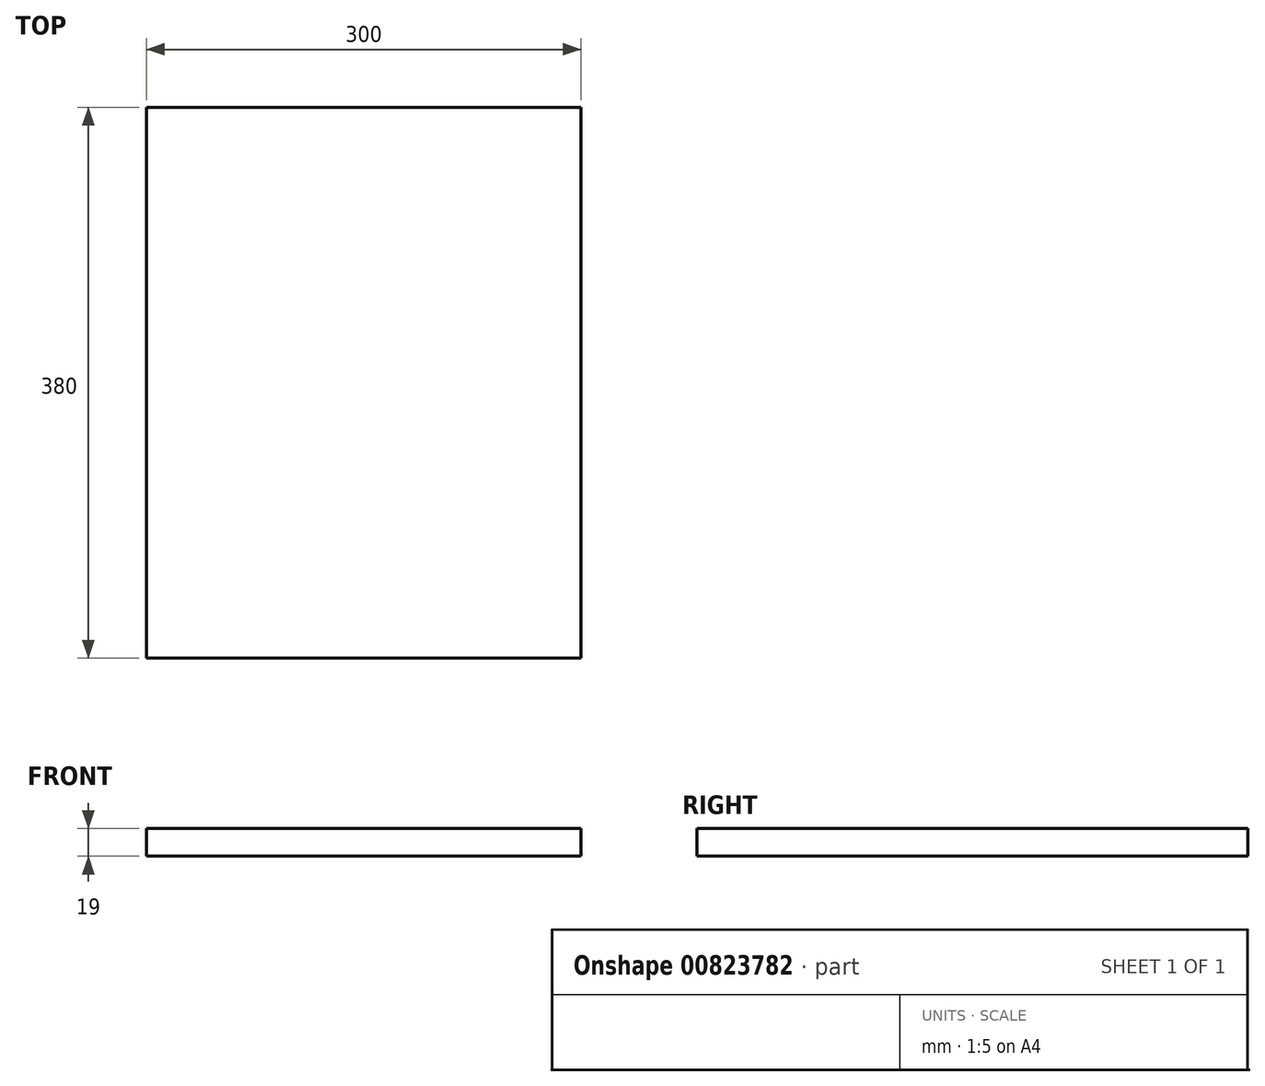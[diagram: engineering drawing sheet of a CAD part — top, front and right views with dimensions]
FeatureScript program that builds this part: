
annotation { "Feature Type Name" : "Feature", "Feature Type Description" : "" }
export const myFeature = defineFeature(function(context is Context, id is Id, definition is map)
    precondition{}
    {
        {
            var Q0;
            Q0=qCreatedBy(makeId("Top.planeOp"),FACE);
            var sketch = newSketch(context, id + "F0", { "sketchPlane" : qUnion([Q0])});
            skLineSegment(sketch, "E0.bottom", {"start": v(150, -190) * mm, "end": v(-150, -190) * mm});
            skLineSegment(sketch, "E0.top", {"start": v(150, 190) * mm, "end": v(-150, 190) * mm});
            skLineSegment(sketch, "E0.left", {"start": v(150, -190) * mm, "end": v(150, 190) * mm});
            skLineSegment(sketch, "E0.right", {"start": v(-150, -190) * mm, "end": v(-150, 190) * mm});
            skPoint(sketch, "E0.middle", {"position": v(0, 0) * mm});
            skSolve(sketch);
        }
        {
            var Q0;
            Q0=makeQuery(id+"F0.imprint","IMPRINT",FACE,{"disambiguationData":[TD([[makeQuery(id+"F0.imprint","IMPRINT",EDGE,{"derivedFrom":sQuery(id+"F0.wireOp",EDGE,"E0.bottom")}),-1.0]])]});
            extrude(context, id + "F1", {"entities" : qUnion([Q0]), "depth" : 19 * mm, "offsetDistance" : 25 * mm});
        }
    });
